# Revit family: Bticino-Portier-IP-Platine de rue
name_source: partatom
category: Equipement électrique
units: mm (PartAtom-declared; Revit-internal decimal feet)

## family parameters
Configuration du panneau = Deux colonnes, circuits au sein
Cote de connecteur circulaire = Utiliser le diamètre
Couper avec des vides une fois chargée = Non
Hôte = Face
Partagée = Non
Point de calcul de pièce = Non
Type d'élément = Tableau de raccordement

## types (6) — shared parameters
Conditions Générale d'Utilisation = https://export.legrand.com
Couleur = Noir
Elévation par défaut = 1100 mm
Fabricant = BTICINO
IK = 07
IP = 54
Mode de pose = Encastré
Site web configurateur = https://www.homesystems-legrandgroup.com
Temperature d'utilisation MIN-MAX = -40/+70 °C
Tension = 24 V DC
Type d'interface = Réseau filaire
Type de raccordement = Câble RJ45

## per-type parameters (varying)
| type | Avec lecteur d'empreinte | Camera | Désignation produit | Ecran Tactile | Hauteur | Hauteur encastrement | Largeur | Largeur encastrement | Modélisation | Référence / Modèle | profondeur d'encastrement |
| PLATINE DE RUE 10" - LECTEUR EMPREINTE | Oui | Avec Caméra | IP - PLATINE DE RUE FULL 10" - LECTEUR EMPREINTE | Oui | 430 mm  [stored 1.41076 ft] | 415 mm  [stored 1.36155 ft] | 195 mm  [stored 0.639764 ft] | 184 mm  [stored 0.603675 ft] | Panel 10'' : 374000 | BT-374000 | 60 mm  [stored 0.19685 ft] |
| PLATINE DE RUE 10" | Non | Avec Caméra | IP - PLATINE DE RUE 10" | Oui | 430 mm  [stored 1.41076 ft] | 415 mm  [stored 1.36155 ft] | 195 mm  [stored 0.639764 ft] | 184 mm  [stored 0.603675 ft] | Panel 10'' : 374002 | BT-374002 | 60 mm  [stored 0.19685 ft] |
| PLATINE DE RUE - CLAVIER - LECTEUR EMPREINTE | Oui | Avec Caméra | IP - PLATINE DE RUE CLAVIER FULL - LECTEUR EMPREINTE | Non | 400 mm  [stored 1.31234 ft] | 384 mm  [stored 1.25984 ft] | 160 mm  [stored 0.524934 ft] | 149 mm  [stored 0.488845 ft] | Panel keypad' : 374001 | BT-374001 | 60 mm  [stored 0.19685 ft] |
| PLATINE DE RUE - CLAVIER | Non | Sans Caméra | IP - PLATINE DE RUE CLAVIER | Non | 400 mm  [stored 1.31234 ft] | 384 mm  [stored 1.25984 ft] | 160 mm  [stored 0.524934 ft] | 149 mm  [stored 0.488845 ft] | Panel keypad' : 374003 | BT-374003 | 60 mm  [stored 0.19685 ft] |
| PLATINE DE RUE PETIT FORMAT AVEC ECRAN | Non | Avec caméra de vision nocturne | IP - PETITE PLATINE DE RUE - ECRAN 4.3" | Oui | 245 mm  [stored 0.803806 ft] | 232 mm  [stored 0.761155 ft] | 92 mm  [stored 0.301837 ft] | 82 mm  [stored 0.269029 ft] | Small panel Touch display : 374005 | BT-374005 | 62 mm  [stored 0.203412 ft] |
| PLATINE DE RUE PETIT FORMAT | Non | Avec Caméra | IP - PETITE PLATINE DE RUE | Non | 193 mm  [stored 0.633202 ft] | 178 mm  [stored 0.58399 ft] | 94 mm  [stored 0.308399 ft] | 84 mm  [stored 0.275591 ft] | Small panel : 374004 | BT-374004 | 59 mm |

note: [stored X ft] marks values corroborated as IEEE doubles in the binary element streams (Revit-internal decimal feet)
